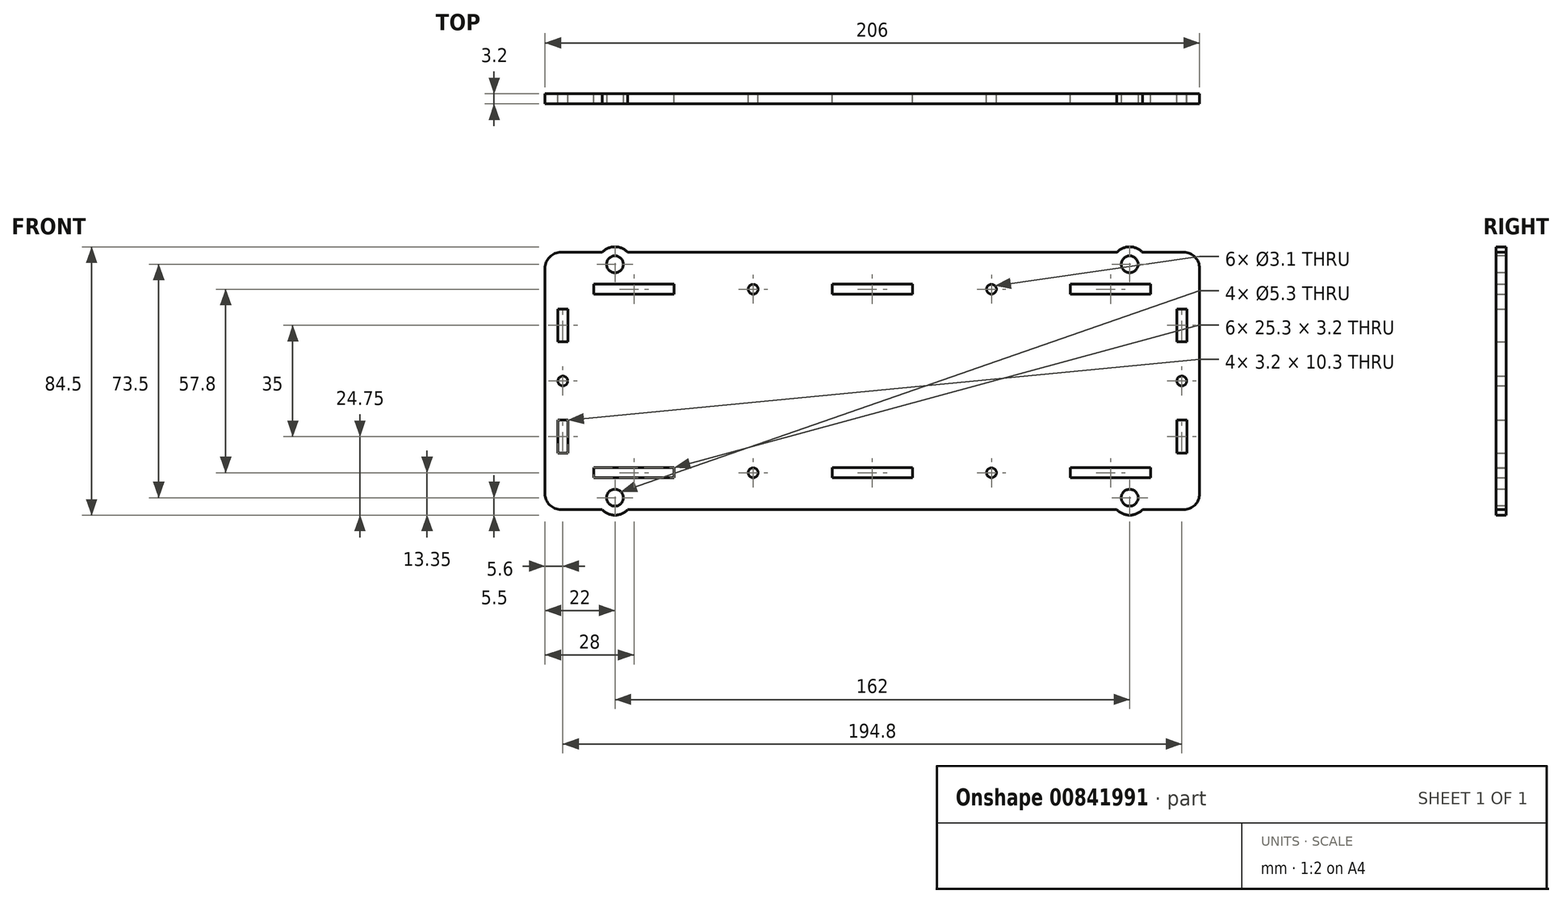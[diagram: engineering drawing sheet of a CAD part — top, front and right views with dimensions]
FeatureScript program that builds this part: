
annotation { "Feature Type Name" : "Feature", "Feature Type Description" : "" }
export const myFeature = defineFeature(function(context is Context, id is Id, definition is map)
    precondition{}
    {
        {
            assignVariable(context, id + "F0", {"name" : "mat_t", "anyValue" : 3.2});
        }
        {
            var Q0;
            Q0=qCreatedBy(makeId("Front.planeOp"),FACE);
            var sketch = newSketch(context, id + "F1", { "sketchPlane" : qUnion([Q0])});
            skLineSegment(sketch, "E0.left", {"start": v(-103, 81) * mm, "end": v(-103, 0) * mm});
            skLineSegment(sketch, "E0.right", {"start": v(103, 81) * mm, "end": v(103, 0) * mm});
            skLineSegment(sketch, "E1", {"start": v(0, 81) * mm, "end": v(0, 0) * mm, "construction": true});
            skLineSegment(sketch, "E2", {"start": v(-99, 81) * mm, "end": v(-99, 0) * mm, "construction": true});
            skLineSegment(sketch, "E3", {"start": v(99, 81) * mm, "end": v(99, 0) * mm, "construction": true});
            skLineSegment(sketch, "E4", {"start": v(-99, 0) * mm, "end": v(99, 0) * mm});
            skLineSegment(sketch, "E5", {"start": v(99, 0) * mm, "end": v(103, 0) * mm});
            skLineSegment(sketch, "E6", {"start": v(-99, 0) * mm, "end": v(-103, 0) * mm});
            skLineSegment(sketch, "E7", {"start": v(-99, 81) * mm, "end": v(99, 81) * mm});
            skLineSegment(sketch, "E8", {"start": v(99, 81) * mm, "end": v(103, 81) * mm});
            skLineSegment(sketch, "E9", {"start": v(-103, 81) * mm, "end": v(-99, 81) * mm});
            skLineSegment(sketch, "E10.bottom", {"start": v(-99, 63.15) * mm, "end": v(-95.8, 63.15) * mm});
            skLineSegment(sketch, "E10.top", {"start": v(-99, 52.85) * mm, "end": v(-95.8, 52.85) * mm});
            skLineSegment(sketch, "E10.left", {"start": v(-99, 63.15) * mm, "end": v(-99, 52.85) * mm});
            skLineSegment(sketch, "E10.right", {"start": v(-95.8, 63.15) * mm, "end": v(-95.8, 52.85) * mm});
            skLineSegment(sketch, "E11", {"start": v(-103, 40.5) * mm, "end": v(103, 40.5) * mm, "construction": true});
            skCircle(sketch, "E12", {"center": v(-97.4, 40.5) * mm, "radius": 1.55 * mm});
            skLineSegment(sketch, "E13", {"start": v(-97.4, 52.85) * mm, "end": v(-97.4, 40.5) * mm, "construction": true});
            skLineSegment(sketch, "E14.MirrorCS", {"start": v(-99, 17.85) * mm, "end": v(-95.8, 17.85) * mm});
            skLineSegment(sketch, "E15.MirrorCS", {"start": v(-99, 17.85) * mm, "end": v(-99, 28.15) * mm});
            skLineSegment(sketch, "E16.MirrorCS", {"start": v(-95.8, 17.85) * mm, "end": v(-95.8, 28.15) * mm});
            skLineSegment(sketch, "E17.MirrorCS", {"start": v(-99, 28.15) * mm, "end": v(-95.8, 28.15) * mm});
            skLineSegment(sketch, "E18.MirrorCS", {"start": v(99, 52.85) * mm, "end": v(95.8, 52.85) * mm});
            skLineSegment(sketch, "E19.MirrorCS", {"start": v(99, 63.15) * mm, "end": v(95.8, 63.15) * mm});
            skCircle(sketch, "E20.MirrorC", {"center": v(97.4, 40.5) * mm, "radius": 1.55 * mm});
            skLineSegment(sketch, "E21.MirrorCS", {"start": v(99, 17.85) * mm, "end": v(95.8, 17.85) * mm});
            skLineSegment(sketch, "E22.MirrorCS", {"start": v(99, 63.15) * mm, "end": v(99, 52.85) * mm});
            skLineSegment(sketch, "E23.MirrorCS", {"start": v(95.8, 63.15) * mm, "end": v(95.8, 52.85) * mm});
            skLineSegment(sketch, "E24.MirrorCS", {"start": v(99, 17.85) * mm, "end": v(99, 28.15) * mm});
            skLineSegment(sketch, "E25.MirrorCS", {"start": v(99, 28.15) * mm, "end": v(95.8, 28.15) * mm});
            skLineSegment(sketch, "E26.MirrorCS", {"start": v(97.4, 52.85) * mm, "end": v(97.4, 40.5) * mm, "construction": true});
            skLineSegment(sketch, "E27.MirrorCS", {"start": v(95.8, 17.85) * mm, "end": v(95.8, 28.15) * mm});
            skLineSegment(sketch, "E28", {"start": v(-103, 71) * mm, "end": v(103, 71) * mm, "construction": true});
            skLineSegment(sketch, "E29.MirrorCS", {"start": v(-103, 10) * mm, "end": v(103, 10) * mm, "construction": true});
            skLineSegment(sketch, "E30.bottom", {"start": v(-12.65, 10) * mm, "end": v(12.65, 10) * mm});
            skLineSegment(sketch, "E30.top", {"start": v(-12.65, 13.2) * mm, "end": v(12.65, 13.2) * mm});
            skLineSegment(sketch, "E30.left", {"start": v(-12.65, 10) * mm, "end": v(-12.65, 13.2) * mm});
            skLineSegment(sketch, "E30.right", {"start": v(12.65, 10) * mm, "end": v(12.65, 13.2) * mm});
            skLineSegment(sketch, "E31.bottom", {"start": v(-87.65, 10) * mm, "end": v(-62.35, 10) * mm});
            skLineSegment(sketch, "E31.top", {"start": v(-87.65, 13.2) * mm, "end": v(-62.35, 13.2) * mm});
            skLineSegment(sketch, "E31.left", {"start": v(-87.65, 10) * mm, "end": v(-87.65, 13.2) * mm});
            skLineSegment(sketch, "E31.right", {"start": v(-62.35, 10) * mm, "end": v(-62.35, 13.2) * mm});
            skLineSegment(sketch, "E32.MirrorCS", {"start": v(87.65, 10) * mm, "end": v(62.35, 10) * mm});
            skLineSegment(sketch, "E33.MirrorCS", {"start": v(62.35, 10) * mm, "end": v(62.35, 13.2) * mm});
            skLineSegment(sketch, "E34.MirrorCS", {"start": v(87.65, 10) * mm, "end": v(87.65, 13.2) * mm});
            skLineSegment(sketch, "E35.MirrorCS", {"start": v(87.65, 13.2) * mm, "end": v(62.35, 13.2) * mm});
            skLineSegment(sketch, "E36", {"start": v(-75, 13.2) * mm, "end": v(-75, 10) * mm, "construction": true});
            skLineSegment(sketch, "E37", {"start": v(75, 13.2) * mm, "end": v(75, 10) * mm, "construction": true});
            skLineSegment(sketch, "E38", {"start": v(-62.35, 11.6) * mm, "end": v(-12.65, 11.6) * mm, "construction": true});
            skCircle(sketch, "E39", {"center": v(-37.5, 11.6) * mm, "radius": 1.55 * mm});
            skCircle(sketch, "E40.MirrorC", {"center": v(37.5, 11.6) * mm, "radius": 1.55 * mm});
            skLineSegment(sketch, "E41", {"start": v(0, 13.2) * mm, "end": v(0, 10) * mm, "construction": true});
            skLineSegment(sketch, "E42.MirrorCS", {"start": v(-12.65, 71) * mm, "end": v(-12.65, 67.8) * mm});
            skLineSegment(sketch, "E43.MirrorCS", {"start": v(-62.35, 71) * mm, "end": v(-62.35, 67.8) * mm});
            skLineSegment(sketch, "E44.MirrorCS", {"start": v(12.65, 71) * mm, "end": v(12.65, 67.8) * mm});
            skLineSegment(sketch, "E45.MirrorCS", {"start": v(-62.35, 69.4) * mm, "end": v(-12.65, 69.4) * mm, "construction": true});
            skCircle(sketch, "E46.MirrorC", {"center": v(37.5, 69.4) * mm, "radius": 1.55 * mm});
            skLineSegment(sketch, "E47.MirrorCS", {"start": v(0, 67.8) * mm, "end": v(0, 71) * mm, "construction": true});
            skLineSegment(sketch, "E48.MirrorCS", {"start": v(-12.65, 67.8) * mm, "end": v(12.65, 67.8) * mm});
            skLineSegment(sketch, "E49.MirrorCS", {"start": v(87.65, 67.8) * mm, "end": v(62.35, 67.8) * mm});
            skLineSegment(sketch, "E50.MirrorCS", {"start": v(-87.65, 71) * mm, "end": v(-87.65, 67.8) * mm});
            skLineSegment(sketch, "E51.MirrorCS", {"start": v(75, 67.8) * mm, "end": v(75, 71) * mm, "construction": true});
            skLineSegment(sketch, "E52.MirrorCS", {"start": v(-87.65, 67.8) * mm, "end": v(-62.35, 67.8) * mm});
            skLineSegment(sketch, "E53.MirrorCS", {"start": v(62.35, 71) * mm, "end": v(62.35, 67.8) * mm});
            skLineSegment(sketch, "E54.MirrorCS", {"start": v(-75, 67.8) * mm, "end": v(-75, 71) * mm, "construction": true});
            skCircle(sketch, "E55.MirrorC", {"center": v(-37.5, 69.4) * mm, "radius": 1.55 * mm});
            skLineSegment(sketch, "E56.MirrorCS", {"start": v(87.65, 71) * mm, "end": v(87.65, 67.8) * mm});
            skLineSegment(sketch, "E57.MirrorCS", {"start": v(-87.65, 71) * mm, "end": v(-62.35, 71) * mm});
            skLineSegment(sketch, "E58.MirrorCS", {"start": v(87.65, 71) * mm, "end": v(62.35, 71) * mm});
            skLineSegment(sketch, "E59.MirrorCS", {"start": v(-12.65, 71) * mm, "end": v(12.65, 71) * mm});
            skLineSegment(sketch, "E60", {"start": v(-99, 23) * mm, "end": v(-95.8, 23) * mm, "construction": true});
            skLineSegment(sketch, "E61", {"start": v(-99, 58) * mm, "end": v(-95.8, 58) * mm, "construction": true});
            skSolve(sketch);
        }
        {
            var Q0;
            Q0 = qSketchRegion(id + "F1", true);
            extrude(context, id + "F2", {"entities" : qUnion([Q0]), "depth" : (getVariable(context, 'mat_t')) * mm, "offsetDistance" : 25 * mm});
        }
        {
            var Q0;
            Q0=makeQuery(id+"F2.opExtrude","CAP_FACE",FACE,{"disambiguationData":[OSD([sQuery(id+"F1.wireOp",EDGE,"E0.left"),sQuery(id+"F1.wireOp",EDGE,"E0.right"),sQuery(id+"F1.wireOp",EDGE,"E4"),sQuery(id+"F1.wireOp",EDGE,"E5"),sQuery(id+"F1.wireOp",EDGE,"E6"),sQuery(id+"F1.wireOp",EDGE,"E7"),sQuery(id+"F1.wireOp",EDGE,"E8"),sQuery(id+"F1.wireOp",EDGE,"E9"),sQuery(id+"F1.wireOp",EDGE,"E10.bottom"),sQuery(id+"F1.wireOp",EDGE,"E10.top"),sQuery(id+"F1.wireOp",EDGE,"E10.left"),sQuery(id+"F1.wireOp",EDGE,"E10.right"),sQuery(id+"F1.wireOp",EDGE,"E12"),sQuery(id+"F1.wireOp",EDGE,"E14.MirrorCS"),sQuery(id+"F1.wireOp",EDGE,"E15.MirrorCS"),sQuery(id+"F1.wireOp",EDGE,"E16.MirrorCS"),sQuery(id+"F1.wireOp",EDGE,"E17.MirrorCS"),sQuery(id+"F1.wireOp",EDGE,"E18.MirrorCS"),sQuery(id+"F1.wireOp",EDGE,"E19.MirrorCS"),sQuery(id+"F1.wireOp",EDGE,"E20.MirrorC"),sQuery(id+"F1.wireOp",EDGE,"E21.MirrorCS"),sQuery(id+"F1.wireOp",EDGE,"E22.MirrorCS"),sQuery(id+"F1.wireOp",EDGE,"E23.MirrorCS"),sQuery(id+"F1.wireOp",EDGE,"E24.MirrorCS"),sQuery(id+"F1.wireOp",EDGE,"E25.MirrorCS"),sQuery(id+"F1.wireOp",EDGE,"E27.MirrorCS"),sQuery(id+"F1.wireOp",EDGE,"E30.bottom"),sQuery(id+"F1.wireOp",EDGE,"E30.top"),sQuery(id+"F1.wireOp",EDGE,"E30.left"),sQuery(id+"F1.wireOp",EDGE,"E30.right"),sQuery(id+"F1.wireOp",EDGE,"E31.bottom"),sQuery(id+"F1.wireOp",EDGE,"E31.top"),sQuery(id+"F1.wireOp",EDGE,"E31.left"),sQuery(id+"F1.wireOp",EDGE,"E31.right"),sQuery(id+"F1.wireOp",EDGE,"E32.MirrorCS"),sQuery(id+"F1.wireOp",EDGE,"E33.MirrorCS"),sQuery(id+"F1.wireOp",EDGE,"E34.MirrorCS"),sQuery(id+"F1.wireOp",EDGE,"E35.MirrorCS"),sQuery(id+"F1.wireOp",EDGE,"E39"),sQuery(id+"F1.wireOp",EDGE,"E40.MirrorC"),sQuery(id+"F1.wireOp",EDGE,"E42.MirrorCS"),sQuery(id+"F1.wireOp",EDGE,"E43.MirrorCS"),sQuery(id+"F1.wireOp",EDGE,"E44.MirrorCS"),sQuery(id+"F1.wireOp",EDGE,"E46.MirrorC"),sQuery(id+"F1.wireOp",EDGE,"E48.MirrorCS"),sQuery(id+"F1.wireOp",EDGE,"E49.MirrorCS"),sQuery(id+"F1.wireOp",EDGE,"E50.MirrorCS"),sQuery(id+"F1.wireOp",EDGE,"E52.MirrorCS"),sQuery(id+"F1.wireOp",EDGE,"E53.MirrorCS"),sQuery(id+"F1.wireOp",EDGE,"E55.MirrorC"),sQuery(id+"F1.wireOp",EDGE,"E56.MirrorCS"),sQuery(id+"F1.wireOp",EDGE,"E57.MirrorCS"),sQuery(id+"F1.wireOp",EDGE,"E58.MirrorCS"),sQuery(id+"F1.wireOp",EDGE,"E59.MirrorCS")])],"isStart":false});
            var sketch = newSketch(context, id + "F3", { "sketchPlane" : qUnion([Q0])});
            skLineSegment(sketch, "E62", {"start": v(-103, 40.5) * mm, "end": v(103, 40.5) * mm, "construction": true});
            skLineSegment(sketch, "E63.bottom", {"start": v(81, 3.75) * mm, "end": v(-81, 3.75) * mm, "construction": true});
            skLineSegment(sketch, "E63.top", {"start": v(81, 77.25) * mm, "end": v(-81, 77.25) * mm, "construction": true});
            skLineSegment(sketch, "E63.left", {"start": v(81, 3.75) * mm, "end": v(81, 77.25) * mm, "construction": true});
            skLineSegment(sketch, "E63.right", {"start": v(-81, 3.75) * mm, "end": v(-81, 77.25) * mm, "construction": true});
            skPoint(sketch, "E63.middle", {"position": v(0, 40.5) * mm});
            skLineSegment(sketch, "E64", {"start": v(0, 77.25) * mm, "end": v(0, 3.75) * mm, "construction": true});
            skCircle(sketch, "E65", {"center": v(-81, 77.25) * mm, "radius": 2.65 * mm});
            skCircle(sketch, "E66.MirrorC", {"center": v(-81, 3.75) * mm, "radius": 2.65 * mm});
            skCircle(sketch, "E67.MirrorC", {"center": v(81, 3.75) * mm, "radius": 2.65 * mm});
            skCircle(sketch, "E68.MirrorC", {"center": v(81, 77.25) * mm, "radius": 2.65 * mm});
            skSolve(sketch);
        }
        {
            var Q0;
            Q0=makeQuery(id+"F2.opExtrude","CAP_FACE",FACE,{"disambiguationData":[OSD([sQuery(id+"F1.wireOp",EDGE,"E0.left"),sQuery(id+"F1.wireOp",EDGE,"E0.right"),sQuery(id+"F1.wireOp",EDGE,"E4"),sQuery(id+"F1.wireOp",EDGE,"E5"),sQuery(id+"F1.wireOp",EDGE,"E6"),sQuery(id+"F1.wireOp",EDGE,"E7"),sQuery(id+"F1.wireOp",EDGE,"E8"),sQuery(id+"F1.wireOp",EDGE,"E9"),sQuery(id+"F1.wireOp",EDGE,"E10.bottom"),sQuery(id+"F1.wireOp",EDGE,"E10.top"),sQuery(id+"F1.wireOp",EDGE,"E10.left"),sQuery(id+"F1.wireOp",EDGE,"E10.right"),sQuery(id+"F1.wireOp",EDGE,"E12"),sQuery(id+"F1.wireOp",EDGE,"E14.MirrorCS"),sQuery(id+"F1.wireOp",EDGE,"E15.MirrorCS"),sQuery(id+"F1.wireOp",EDGE,"E16.MirrorCS"),sQuery(id+"F1.wireOp",EDGE,"E17.MirrorCS"),sQuery(id+"F1.wireOp",EDGE,"E18.MirrorCS"),sQuery(id+"F1.wireOp",EDGE,"E19.MirrorCS"),sQuery(id+"F1.wireOp",EDGE,"E20.MirrorC"),sQuery(id+"F1.wireOp",EDGE,"E21.MirrorCS"),sQuery(id+"F1.wireOp",EDGE,"E22.MirrorCS"),sQuery(id+"F1.wireOp",EDGE,"E23.MirrorCS"),sQuery(id+"F1.wireOp",EDGE,"E24.MirrorCS"),sQuery(id+"F1.wireOp",EDGE,"E25.MirrorCS"),sQuery(id+"F1.wireOp",EDGE,"E27.MirrorCS"),sQuery(id+"F1.wireOp",EDGE,"E30.bottom"),sQuery(id+"F1.wireOp",EDGE,"E30.top"),sQuery(id+"F1.wireOp",EDGE,"E30.left"),sQuery(id+"F1.wireOp",EDGE,"E30.right"),sQuery(id+"F1.wireOp",EDGE,"E31.bottom"),sQuery(id+"F1.wireOp",EDGE,"E31.top"),sQuery(id+"F1.wireOp",EDGE,"E31.left"),sQuery(id+"F1.wireOp",EDGE,"E31.right"),sQuery(id+"F1.wireOp",EDGE,"E32.MirrorCS"),sQuery(id+"F1.wireOp",EDGE,"E33.MirrorCS"),sQuery(id+"F1.wireOp",EDGE,"E34.MirrorCS"),sQuery(id+"F1.wireOp",EDGE,"E35.MirrorCS"),sQuery(id+"F1.wireOp",EDGE,"E39"),sQuery(id+"F1.wireOp",EDGE,"E40.MirrorC"),sQuery(id+"F1.wireOp",EDGE,"E42.MirrorCS"),sQuery(id+"F1.wireOp",EDGE,"E43.MirrorCS"),sQuery(id+"F1.wireOp",EDGE,"E44.MirrorCS"),sQuery(id+"F1.wireOp",EDGE,"E46.MirrorC"),sQuery(id+"F1.wireOp",EDGE,"E48.MirrorCS"),sQuery(id+"F1.wireOp",EDGE,"E49.MirrorCS"),sQuery(id+"F1.wireOp",EDGE,"E50.MirrorCS"),sQuery(id+"F1.wireOp",EDGE,"E52.MirrorCS"),sQuery(id+"F1.wireOp",EDGE,"E53.MirrorCS"),sQuery(id+"F1.wireOp",EDGE,"E55.MirrorC"),sQuery(id+"F1.wireOp",EDGE,"E56.MirrorCS"),sQuery(id+"F1.wireOp",EDGE,"E57.MirrorCS"),sQuery(id+"F1.wireOp",EDGE,"E58.MirrorCS"),sQuery(id+"F1.wireOp",EDGE,"E59.MirrorCS")])],"isStart":false});
            var sketch = newSketch(context, id + "F4", { "sketchPlane" : qUnion([Q0])});
            skCircle(sketch, "E69", {"center": v(-81, 77.25) * mm, "radius": 5.5 * mm});
            skCircle(sketch, "E70.MirrorC", {"center": v(81, 77.25) * mm, "radius": 5.5 * mm});
            skCircle(sketch, "E71.MirrorC", {"center": v(81, 3.75) * mm, "radius": 5.5 * mm});
            skCircle(sketch, "E72.MirrorC", {"center": v(-81, 3.75) * mm, "radius": 5.5 * mm});
            skSolve(sketch);
        }
        {
            var Q0;
            Q0 = qSketchRegion(id + "F4", true);
            var Q1;
            Q1=makeQuery(id+"F2.opExtrude","CAP_FACE",FACE,{"disambiguationData":[OSD([sQuery(id+"F1.wireOp",EDGE,"E0.left"),sQuery(id+"F1.wireOp",EDGE,"E0.right"),sQuery(id+"F1.wireOp",EDGE,"E4"),sQuery(id+"F1.wireOp",EDGE,"E5"),sQuery(id+"F1.wireOp",EDGE,"E6"),sQuery(id+"F1.wireOp",EDGE,"E7"),sQuery(id+"F1.wireOp",EDGE,"E8"),sQuery(id+"F1.wireOp",EDGE,"E9"),sQuery(id+"F1.wireOp",EDGE,"E10.bottom"),sQuery(id+"F1.wireOp",EDGE,"E10.top"),sQuery(id+"F1.wireOp",EDGE,"E10.left"),sQuery(id+"F1.wireOp",EDGE,"E10.right"),sQuery(id+"F1.wireOp",EDGE,"E12"),sQuery(id+"F1.wireOp",EDGE,"E14.MirrorCS"),sQuery(id+"F1.wireOp",EDGE,"E15.MirrorCS"),sQuery(id+"F1.wireOp",EDGE,"E16.MirrorCS"),sQuery(id+"F1.wireOp",EDGE,"E17.MirrorCS"),sQuery(id+"F1.wireOp",EDGE,"E18.MirrorCS"),sQuery(id+"F1.wireOp",EDGE,"E19.MirrorCS"),sQuery(id+"F1.wireOp",EDGE,"E20.MirrorC"),sQuery(id+"F1.wireOp",EDGE,"E21.MirrorCS"),sQuery(id+"F1.wireOp",EDGE,"E22.MirrorCS"),sQuery(id+"F1.wireOp",EDGE,"E23.MirrorCS"),sQuery(id+"F1.wireOp",EDGE,"E24.MirrorCS"),sQuery(id+"F1.wireOp",EDGE,"E25.MirrorCS"),sQuery(id+"F1.wireOp",EDGE,"E27.MirrorCS"),sQuery(id+"F1.wireOp",EDGE,"E30.bottom"),sQuery(id+"F1.wireOp",EDGE,"E30.top"),sQuery(id+"F1.wireOp",EDGE,"E30.left"),sQuery(id+"F1.wireOp",EDGE,"E30.right"),sQuery(id+"F1.wireOp",EDGE,"E31.bottom"),sQuery(id+"F1.wireOp",EDGE,"E31.top"),sQuery(id+"F1.wireOp",EDGE,"E31.left"),sQuery(id+"F1.wireOp",EDGE,"E31.right"),sQuery(id+"F1.wireOp",EDGE,"E32.MirrorCS"),sQuery(id+"F1.wireOp",EDGE,"E33.MirrorCS"),sQuery(id+"F1.wireOp",EDGE,"E34.MirrorCS"),sQuery(id+"F1.wireOp",EDGE,"E35.MirrorCS"),sQuery(id+"F1.wireOp",EDGE,"E39"),sQuery(id+"F1.wireOp",EDGE,"E40.MirrorC"),sQuery(id+"F1.wireOp",EDGE,"E42.MirrorCS"),sQuery(id+"F1.wireOp",EDGE,"E43.MirrorCS"),sQuery(id+"F1.wireOp",EDGE,"E44.MirrorCS"),sQuery(id+"F1.wireOp",EDGE,"E46.MirrorC"),sQuery(id+"F1.wireOp",EDGE,"E48.MirrorCS"),sQuery(id+"F1.wireOp",EDGE,"E49.MirrorCS"),sQuery(id+"F1.wireOp",EDGE,"E50.MirrorCS"),sQuery(id+"F1.wireOp",EDGE,"E52.MirrorCS"),sQuery(id+"F1.wireOp",EDGE,"E53.MirrorCS"),sQuery(id+"F1.wireOp",EDGE,"E55.MirrorC"),sQuery(id+"F1.wireOp",EDGE,"E56.MirrorCS"),sQuery(id+"F1.wireOp",EDGE,"E57.MirrorCS"),sQuery(id+"F1.wireOp",EDGE,"E58.MirrorCS"),sQuery(id+"F1.wireOp",EDGE,"E59.MirrorCS")])],"isStart":true});
            extrude(context, id + "F5", {"entities" : qUnion([Q0]), "operationType" : NewBodyOperationType.ADD, "endBound" : BoundingType.UP_TO_SURFACE, "oppositeDirection" : true, "depth" : 25 * mm, "endBoundEntityFace" : qUnion([Q1]), "offsetDistance" : 25 * mm});
        }
        {
            var Q0;
            Q0 = qSketchRegion(id + "F3", true);
            extrude(context, id + "F6", {"entities" : qUnion([Q0]), "operationType" : NewBodyOperationType.REMOVE, "endBound" : BoundingType.THROUGH_ALL, "oppositeDirection" : true, "depth" : 25 * mm, "offsetDistance" : 25 * mm});
        }
        {
            var Q0;
            Q0=makeQuery(id+"F2.opExtrude","SWEPT_EDGE",EDGE,{"disambiguationData":[OSD([sQuery(id+"F1.wireOp",EDGE,"E0.left"),sQuery(id+"F1.wireOp",EDGE,"E9")])]});
            var Q1;
            Q1=makeQuery(id+"F2.opExtrude","SWEPT_EDGE",EDGE,{"disambiguationData":[OSD([sQuery(id+"F1.wireOp",EDGE,"E0.left"),sQuery(id+"F1.wireOp",EDGE,"E6")])]});
            var Q2;
            Q2=makeQuery(id+"F2.opExtrude","SWEPT_EDGE",EDGE,{"disambiguationData":[OSD([sQuery(id+"F1.wireOp",EDGE,"E0.right"),sQuery(id+"F1.wireOp",EDGE,"E5")])]});
            var Q3;
            Q3=makeQuery(id+"F2.opExtrude","SWEPT_EDGE",EDGE,{"disambiguationData":[OSD([sQuery(id+"F1.wireOp",EDGE,"E0.right"),sQuery(id+"F1.wireOp",EDGE,"E8")])]});
            fillet(context, id + "F7", {"entities" : qUnion([Q0, Q1, Q2, Q3]), "radius" : 5 * mm, "tangentPropagation" : true, "allowEdgeOverflow" : false});
        }
    });
